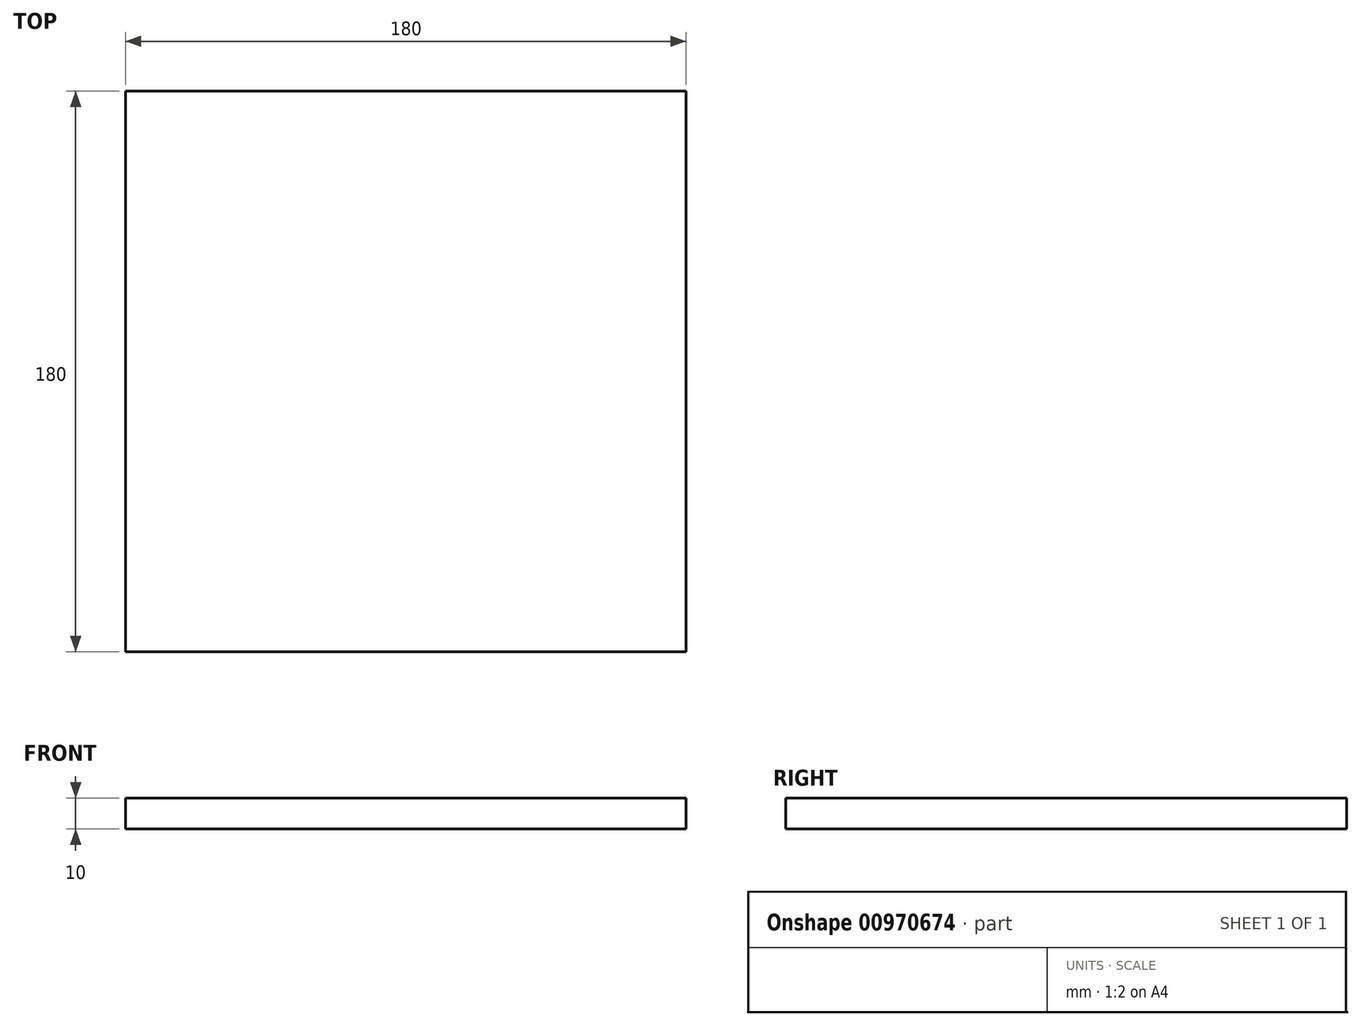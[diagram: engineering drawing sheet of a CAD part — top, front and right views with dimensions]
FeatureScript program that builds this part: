
annotation { "Feature Type Name" : "Feature", "Feature Type Description" : "" }
export const myFeature = defineFeature(function(context is Context, id is Id, definition is map)
    precondition{}
    {
        {
            var Q0;
            Q0=qCreatedBy(makeId("Top.planeOp"),FACE);
            var sketch = newSketch(context, id + "F0", { "sketchPlane" : qUnion([Q0])});
            skLineSegment(sketch, "E0.bottom", {"start": v(-86.4, 112.57) * mm, "end": v(93.6, 112.57) * mm});
            skLineSegment(sketch, "E0.top", {"start": v(-86.4, -67.43) * mm, "end": v(93.6, -67.43) * mm});
            skLineSegment(sketch, "E0.left", {"start": v(-86.4, 112.57) * mm, "end": v(-86.4, -67.43) * mm});
            skLineSegment(sketch, "E0.right", {"start": v(93.6, 112.57) * mm, "end": v(93.6, -67.43) * mm});
            skSolve(sketch);
        }
        {
            var Q0;
            Q0 = qSketchRegion(id + "F0", true);
            extrude(context, id + "F1", {"entities" : qUnion([Q0]), "depth" : 10 * mm, "offsetDistance" : 25.4 * mm});
        }
    });
